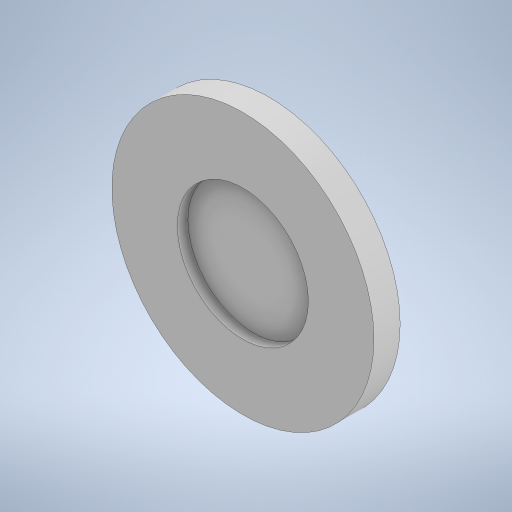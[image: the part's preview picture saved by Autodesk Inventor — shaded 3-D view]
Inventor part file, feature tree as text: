
AUTODESK INVENTOR PART (.ipt)
format: ipt  version: 2023.1 (Build 271208000, 208)  size: 225,280 bytes
history: native  units: mm
features: extrude x2, sketch x2
ambient origin geometry x8: Origin, YZ Plane, XZ Plane, XY Plane, X Axis, Y Axis, Z Axis, Center Point
bodies: Solid1 (feature_tree)
feature tree (4):
  extrude  "Extrusion1"  Depth=5.0mm TaperAngle=0.0deg
  extrude  "Extrusion2"  Depth=2.0mm TaperAngle=0.0deg
  sketch  "Sketch1"  dims[d0=50.0mm d1=5.0mm d2=0.0mm]
  sketch  "Sketch2"  dims[d3=25.0mm d4=2.0mm d5=0.0mm]
